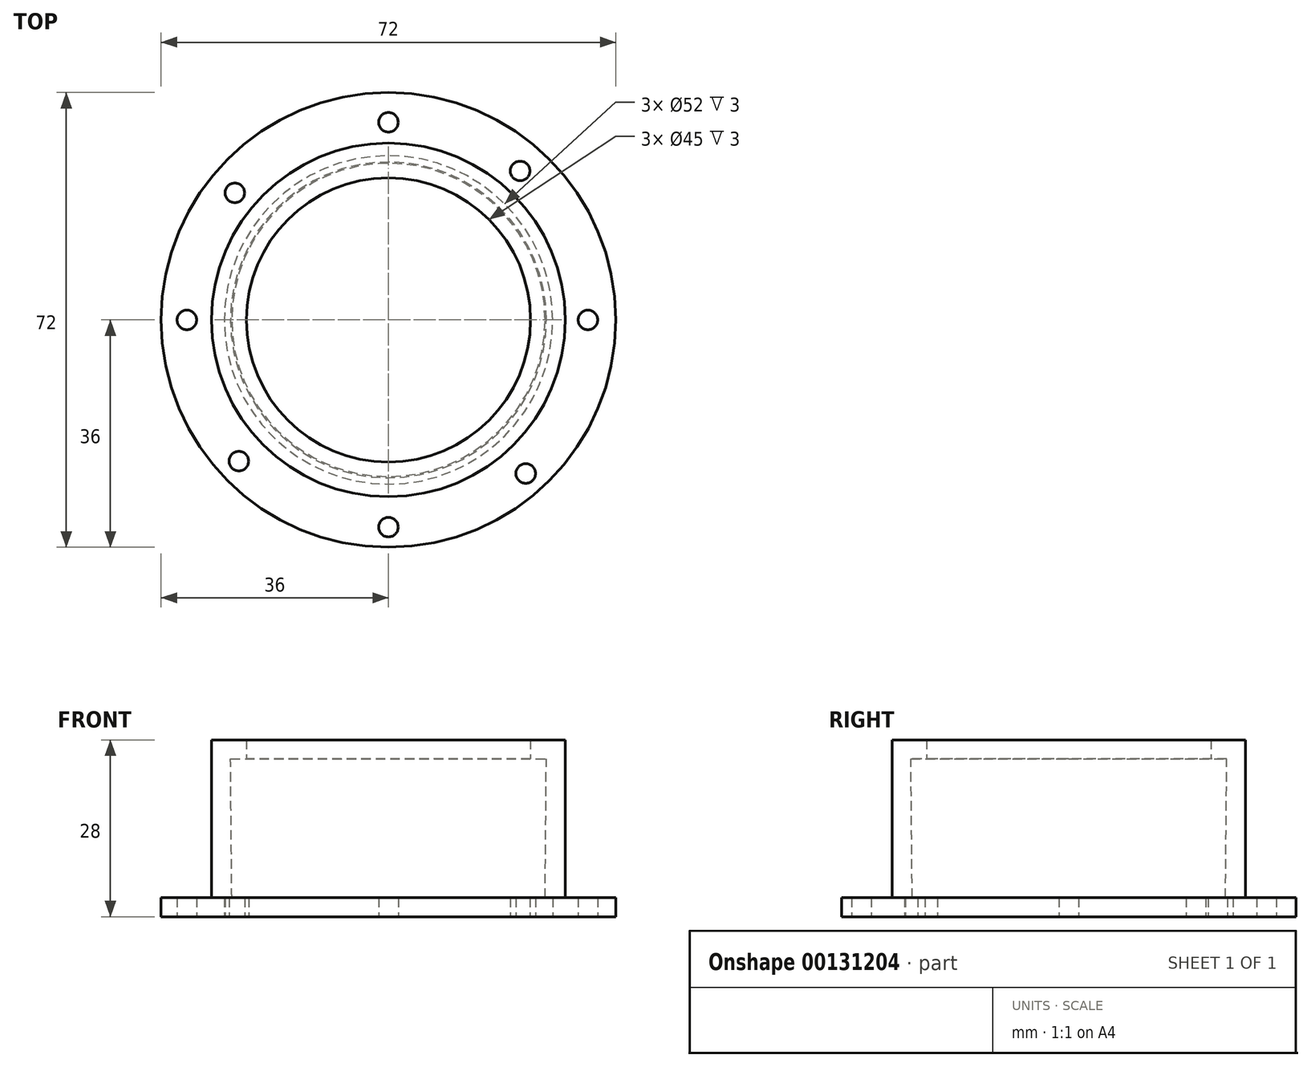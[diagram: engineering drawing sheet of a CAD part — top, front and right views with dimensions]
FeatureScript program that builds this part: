
annotation { "Feature Type Name" : "Feature", "Feature Type Description" : "" }
export const myFeature = defineFeature(function(context is Context, id is Id, definition is map)
    precondition{}
    {
        {
            var Q0;
            Q0=qCreatedBy(makeId("Right.planeOp"),FACE);
            var sketch = newSketch(context, id + "F0", { "sketchPlane" : qUnion([Q0])});
            skLineSegment(sketch, "E0", {"start": v(0, 0) * mm, "end": v(-28, 0) * mm});
            skLineSegment(sketch, "E1", {"start": v(-28, 0) * mm, "end": v(-28, -25) * mm});
            skLineSegment(sketch, "E2", {"start": v(-28, -25) * mm, "end": v(-36, -25) * mm});
            skLineSegment(sketch, "E3", {"start": v(-36, -25) * mm, "end": v(-36, -28) * mm});
            skLineSegment(sketch, "E4", {"start": v(-25, -3) * mm, "end": v(0, -3) * mm});
            skLineSegment(sketch, "E5", {"start": v(0, -3) * mm, "end": v(0, 0) * mm});
            skPoint(sketch, "E6", {"position": v(-28, 0) * mm});
            skPoint(sketch, "E7", {"position": v(-17.04, 0) * mm});
            skLineSegment(sketch, "E8", {"start": v(-36, -28) * mm, "end": v(-26, -28) * mm});
            skLineSegment(sketch, "E9", {"start": v(-26, -28) * mm, "end": v(-26, -25) * mm});
            skLineSegment(sketch, "E10", {"start": v(-26, -25) * mm, "end": v(-24.8, -25) * mm});
            skLineSegment(sketch, "E11", {"start": v(-24.8, -25) * mm, "end": v(-25, -3) * mm});
            skSolve(sketch);
        }
        {
            var Q0;
            Q0 = qSketchRegion(id + "F0", true);
            var Q1;
            Q1=makeQuery(id+"F0.imprint","IMPRINT",FACE,{"disambiguationData":[TD([[makeQuery(id+"F0.imprint","IMPRINT",EDGE,{"derivedFrom":sQuery(id+"F0.wireOp",EDGE,"E0")}),1.0]])]});
            var Q2;
            Q2=sQuery(id+"F0.wireOp",EDGE,"E5");
            revolve(context, id + "F1", {"entities" : qUnion([Q0, Q1]), "axis" : qUnion([Q2]), "revolveType" : RevolveType.FULL});
        }
        {
            var Q0;
            Q0=makeQuery(id+"F1.opRevolve","SWEPT_FACE",FACE,{"disambiguationData":[OSD([sQuery(id+"F0.wireOp",EDGE,"E0")])]});
            var sketch = newSketch(context, id + "F2", { "sketchPlane" : qUnion([Q0])});
            skCircle(sketch, "E12", {"center": v(0, 0) * mm, "radius": 19 * mm});
            skSolve(sketch);
        }
        {
            var Q0;
            Q0=sQuery(id+"F2.wireOp",VERTEX,"E12.center");
            var Q1;
            Q1=makeQuery(id+"F1.opRevolve","SWEPT_BODY",BODY,{"disambiguationData":[OSD([sQuery(id+"F0.wireOp",EDGE,"E0"),sQuery(id+"F0.wireOp",EDGE,"E1"),sQuery(id+"F0.wireOp",EDGE,"E2"),sQuery(id+"F0.wireOp",EDGE,"E3"),sQuery(id+"F0.wireOp",EDGE,"55VT88SI-HALF-vJtD-Bg9c-gAHZYVfEPgCH"),sQuery(id+"F0.wireOp",EDGE,"5bAq7N60-oYln-fniL-s3CO-pV1vLaG9MPB4"),sQuery(id+"F0.wireOp",EDGE,"E4"),sQuery(id+"F0.wireOp",EDGE,"E5")])]});
            hole(context, id + "F3", {"style" : HoleStyle.SIMPLE, "endStyle" : HoleEndStyle.THROUGH, "holeDiameter" : 45 * mm, "locations" : qUnion([Q0]), "scope" : qUnion([Q1]), "isTappedThrough" : true});
        }
        {
            var Q0;
            Q0=makeQuery(id+"F1.opRevolve","SWEPT_FACE",FACE,{"disambiguationData":[OSD([sQuery(id+"F0.wireOp",EDGE,"E2")])]});
            var sketch = newSketch(context, id + "F4", { "sketchPlane" : qUnion([Q0])});
            skCircle(sketch, "E13", {"center": v(0, -32.81) * mm, "radius": 2 * mm});
            skCircle(sketch, "E14", {"center": v(0, 31.3) * mm, "radius": 2 * mm});
            skCircle(sketch, "E15", {"center": v(-31.91, 0) * mm, "radius": 2 * mm});
            skCircle(sketch, "E16", {"center": v(31.58, 0) * mm, "radius": 2 * mm});
            skCircle(sketch, "E17", {"center": v(20.85, 23.59) * mm, "radius": 2 * mm});
            skCircle(sketch, "E18", {"center": v(21.74, -24.31) * mm, "radius": 2 * mm});
            skCircle(sketch, "E19", {"center": v(-24.32, 20.12) * mm, "radius": 2 * mm});
            skCircle(sketch, "E20", {"center": v(-23.68, -22.36) * mm, "radius": 2 * mm});
            skCircle(sketch, "E21", {"center": v(0, -0.76) * mm, "radius": 32.05 * mm, "construction": true});
            skSolve(sketch);
        }
        {
            var Q0;
            Q0=sQuery(id+"F4.wireOp",VERTEX,"E20.center");
            var Q1;
            Q1=sQuery(id+"F4.wireOp",VERTEX,"E15.center");
            var Q2;
            Q2=sQuery(id+"F4.wireOp",VERTEX,"E19.center");
            var Q3;
            Q3=sQuery(id+"F4.wireOp",VERTEX,"E14.center");
            var Q4;
            Q4=sQuery(id+"F4.wireOp",VERTEX,"E17.center");
            var Q5;
            Q5=sQuery(id+"F4.wireOp",VERTEX,"E16.center");
            var Q6;
            Q6=sQuery(id+"F4.wireOp",VERTEX,"E18.center");
            var Q7;
            Q7=sQuery(id+"F4.wireOp",VERTEX,"E13.center");
            var Q8;
            Q8=makeQuery(id+"F1.opRevolve","SWEPT_BODY",BODY,{"disambiguationData":[OSD([sQuery(id+"F0.wireOp",EDGE,"E0"),sQuery(id+"F0.wireOp",EDGE,"E1"),sQuery(id+"F0.wireOp",EDGE,"E2"),sQuery(id+"F0.wireOp",EDGE,"E3"),sQuery(id+"F0.wireOp",EDGE,"55VT88SI-HALF-vJtD-Bg9c-gAHZYVfEPgCH"),sQuery(id+"F0.wireOp",EDGE,"5bAq7N60-oYln-fniL-s3CO-pV1vLaG9MPB4"),sQuery(id+"F0.wireOp",EDGE,"E4"),sQuery(id+"F0.wireOp",EDGE,"E5")])]});
            hole(context, id + "F5", {"style" : HoleStyle.SIMPLE, "endStyle" : HoleEndStyle.THROUGH, "holeDiameter" : 3.1 * mm, "locations" : qUnion([Q0, Q1, Q2, Q3, Q4, Q5, Q6, Q7]), "scope" : qUnion([Q8]), "isTappedThrough" : true});
        }
    });
